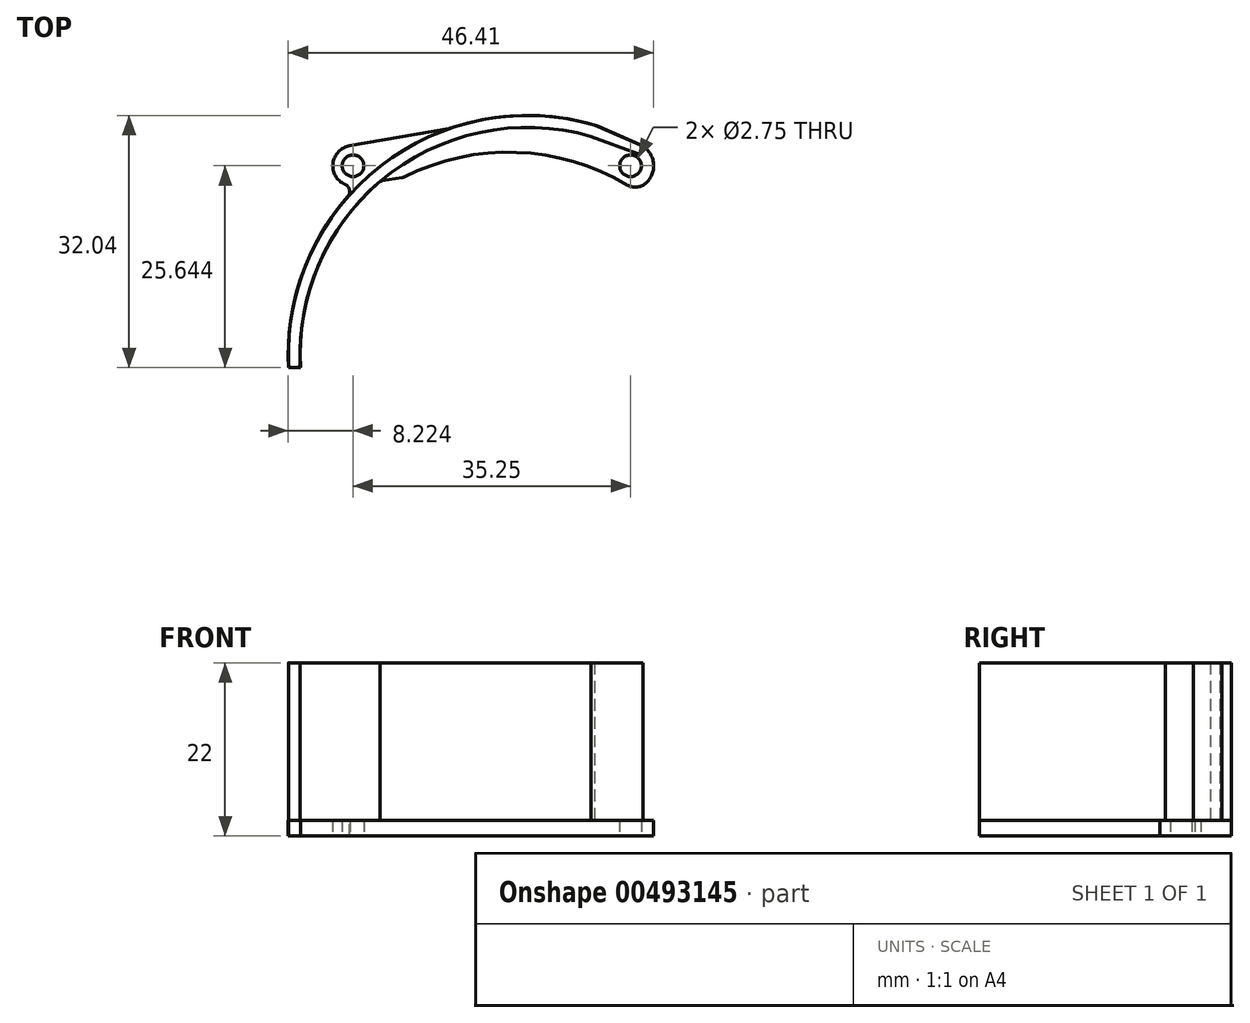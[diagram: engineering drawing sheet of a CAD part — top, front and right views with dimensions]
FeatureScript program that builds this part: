
annotation { "Feature Type Name" : "Feature", "Feature Type Description" : "" }
export const myFeature = defineFeature(function(context is Context, id is Id, definition is map)
    precondition{}
    {
        {
            var Q0;
            Q0=qCreatedBy(makeId("Top.planeOp"),FACE);
            var sketch = newSketch(context, id + "F0", { "sketchPlane" : qUnion([Q0])});
            skCircle(sketch, "E0", {"center": v(-38.27, 2.91) * mm, "radius": 1.38 * mm});
            skCircle(sketch, "E1", {"center": v(-3.02, 2.91) * mm, "radius": 1.38 * mm});
            skArc(sketch, "E2", {"start": v(-38.66, 5.45) * mm, "mid": v(-40.78, 2.37) * mm, "end": v(-37.57, 0.44) * mm});
            skLineSegment(sketch, "E3", {"start": v(-34.78, 0.97) * mm, "end": v(-31.9, 1.44) * mm});
            skPoint(sketch, "E4.left.start.orphan", {"position": v(-41, 0) * mm});
            skArc(sketch, "E5", {"start": v(-2.66, 0) * mm, "mid": v(-0.11, 2.48) * mm, "end": v(-1.83, 5.6) * mm});
            skLineSegment(sketch, "E6", {"start": v(-1.83, 5.6) * mm, "end": v(-7.29, 8) * mm});
            skPoint(sketch, "E4.right.end.orphan", {"position": v(0, 8) * mm});
            skArc(sketch, "E7", {"start": v(-7.29, 8) * mm, "mid": v(-34.87, 2.83) * mm, "end": v(-46.44, -22.73) * mm});
            skArc(sketch, "E8.0", {"start": v(-7.72, 6.56) * mm, "mid": v(-33.98, 1.63) * mm, "end": v(-44.94, -22.73) * mm});
            skLineSegment(sketch, "E9", {"start": v(-7.72, 6.56) * mm, "end": v(-1.83, 4.77) * mm});
            skLineSegment(sketch, "E10", {"start": v(-1.83, 4.77) * mm, "end": v(-1.83, 5.6) * mm});
            skArc(sketch, "E11", {"start": v(-2.66, 0) * mm, "mid": v(-17.1, 4.6) * mm, "end": v(-31.9, 1.44) * mm});
            skPoint(sketch, "E12.end.orphan", {"position": v(-29.03, 1.9) * mm});
            skLineSegment(sketch, "E13", {"start": v(-38.66, 5.45) * mm, "end": v(-26, 7.66) * mm});
            skLineSegment(sketch, "E14", {"start": v(-46.44, -22.73) * mm, "end": v(-44.94, -22.73) * mm});
            skSolve(sketch);
        }
        {
            var Q0;
            Q0 = qSketchRegion(id + "F0", true);
            extrude(context, id + "F1", {"entities" : qUnion([Q0]), "depth" : 2 * mm});
        }
        {
            var Q0;
            Q0=makeQuery(id+"F1.opExtrude","SWEPT_EDGE",EDGE,{"disambiguationData":[OSD([sQuery(id+"F0.wireOp",EDGE,"E5"),sQuery(id+"F0.wireOp",EDGE,"E11")])]});
            fillet(context, id + "F2", {"entities" : qUnion([Q0]), "radius" : 2 * mm, "tangentPropagation" : true, "allowEdgeOverflow" : false});
        }
        {
            var Q0;
            Q0=makeQuery(id+"F1.opExtrude","SWEPT_EDGE",EDGE,{"disambiguationData":[OSD([sQuery(id+"F0.wireOp",EDGE,"E7"),sQuery(id+"F0.wireOp",EDGE,"E13")])]});
            var Q1;
            Q1=makeQuery(id+"F1.opExtrude","SWEPT_EDGE",EDGE,{"disambiguationData":[OSD([sQuery(id+"F0.wireOp",EDGE,"E3"),sQuery(id+"F0.wireOp",EDGE,"E11")])]});
            var Q2;
            Q2=makeQuery(id+"F1.opExtrude","SWEPT_EDGE",EDGE,{"disambiguationData":[OSD([sQuery(id+"F0.wireOp",EDGE,"E3"),sQuery(id+"F0.wireOp",EDGE,"E8.0")])]});
            var Q3;
            Q3=makeQuery(id+"F1.opExtrude","SWEPT_EDGE",EDGE,{"disambiguationData":[OSD([sQuery(id+"F0.wireOp",EDGE,"E2"),sQuery(id+"F0.wireOp",EDGE,"E7")])]});
            fillet(context, id + "F3", {"entities" : qUnion([Q0, Q1, Q2, Q3]), "radius" : 1 * mm, "tangentPropagation" : true, "allowEdgeOverflow" : false});
        }
        {
            var Q0;
            Q0=makeQuery(id+"F1.opExtrude","SWEPT_EDGE",EDGE,{"disambiguationData":[OSD([sQuery(id+"F0.wireOp",EDGE,"E6"),sQuery(id+"F0.wireOp",EDGE,"E7")])]});
            var Q1;
            {var subQ0=sQuery(id+"F0.wireOp",EDGE,"E13");Q1=makeQuery(id+"F3.opFillet","BLEND_EDGE",EDGE,{"blendedFrom":[makeQuery(id+"F1.opExtrude","SWEPT_EDGE",EDGE,{"disambiguationData":[OSD([sQuery(id+"F0.wireOp",EDGE,"E7"),subQ0])]}),makeQuery(id+"F1.opExtrude","SWEPT_FACE",FACE,{"disambiguationData":[OSD([subQ0])]})],"blendedInto":[makeQuery(id+"F1.opExtrude","SWEPT_FACE",FACE,{"disambiguationData":[OSD([subQ0])]})]});}
            fillet(context, id + "F4", {"entities" : qUnion([Q0, Q1]), "radius" : 5 * mm, "tangentPropagation" : true, "allowEdgeOverflow" : false});
        }
        {
            var Q0;
            Q0=makeQuery(id+"F1.opExtrude","CAP_FACE",FACE,{"disambiguationData":[OSD([sQuery(id+"F0.wireOp",EDGE,"E0"),sQuery(id+"F0.wireOp",EDGE,"E1"),sQuery(id+"F0.wireOp",EDGE,"E2"),sQuery(id+"F0.wireOp",EDGE,"E3"),sQuery(id+"F0.wireOp",EDGE,"E5"),sQuery(id+"F0.wireOp",EDGE,"E6"),sQuery(id+"F0.wireOp",EDGE,"E7"),sQuery(id+"F0.wireOp",EDGE,"E8.0"),sQuery(id+"F0.wireOp",EDGE,"E11"),sQuery(id+"F0.wireOp",EDGE,"E13"),sQuery(id+"F0.wireOp",EDGE,"E14")])],"isStart":false});
            var sketch = newSketch(context, id + "F5", { "sketchPlane" : qUnion([Q0])});
            skArc(sketch, "E15", {"start": v(-7.62, 8.1) * mm, "mid": v(-35, 2.71) * mm, "end": v(-46.44, -22.73) * mm});
            skArc(sketch, "E16.0", {"start": v(-8.03, 6.66) * mm, "mid": v(-34.06, 1.54) * mm, "end": v(-44.95, -22.65) * mm});
            skLineSegment(sketch, "E17", {"start": v(-46.44, -22.73) * mm, "end": v(-44.94, -22.73) * mm});
            skLineSegment(sketch, "E18", {"start": v(-8.03, 6.66) * mm, "end": v(-1.45, 4.24) * mm});
            skLineSegment(sketch, "E19", {"start": v(-1.45, 4.24) * mm, "end": v(-1.45, 5.4) * mm});
            skLineSegment(sketch, "E20", {"start": v(-1.45, 5.4) * mm, "end": v(-7.62, 8.1) * mm});
            skSolve(sketch);
        }
        {
            var Q0;
            Q0 = qSketchRegion(id + "F5", true);
            var Q1;
            Q1=makeQuery(id+"F5.imprint","IMPRINT",FACE,{"disambiguationData":[TD([[makeQuery(id+"F5.imprint","IMPRINT",EDGE,{"derivedFrom":sQuery(id+"F5.wireOp",EDGE,"E15")}),1.0]])]});
            extrude(context, id + "F6", {"entities" : qUnion([Q0, Q1]), "depth" : 20 * mm});
        }
        {
            var Q0;
            Q0=makeQuery(id+"F6.opExtrude","SWEPT_EDGE",EDGE,{"disambiguationData":[OSD([sQuery(id+"F5.wireOp",EDGE,"E18"),sQuery(id+"F5.wireOp",EDGE,"E19")])]});
            var Q1;
            Q1=makeQuery(id+"F6.opExtrude","SWEPT_EDGE",EDGE,{"disambiguationData":[OSD([sQuery(id+"F0.wireOp",EDGE,"E5"),sQuery(id+"F5.wireOp",EDGE,"E19"),sQuery(id+"F5.wireOp",EDGE,"E20")])]});
            var Q2;
            Q2=makeQuery(id+"F6.opExtrude","SWEPT_EDGE",EDGE,{"disambiguationData":[OSD([sQuery(id+"F0.wireOp",EDGE,"E8.0"),sQuery(id+"F5.wireOp",EDGE,"E17")])]});
            var Q3;
            Q3=makeQuery(id+"F6.opExtrude","SWEPT_EDGE",EDGE,{"disambiguationData":[OSD([sQuery(id+"F0.wireOp",EDGE,"E7"),sQuery(id+"F5.wireOp",EDGE,"E15"),sQuery(id+"F5.wireOp",EDGE,"E17")])]});
            fillet(context, id + "F7", {"entities" : qUnion([Q0, Q1, Q2, Q3]), "radius" : 0.5 * mm, "tangentPropagation" : true, "allowEdgeOverflow" : false});
        }
    });
